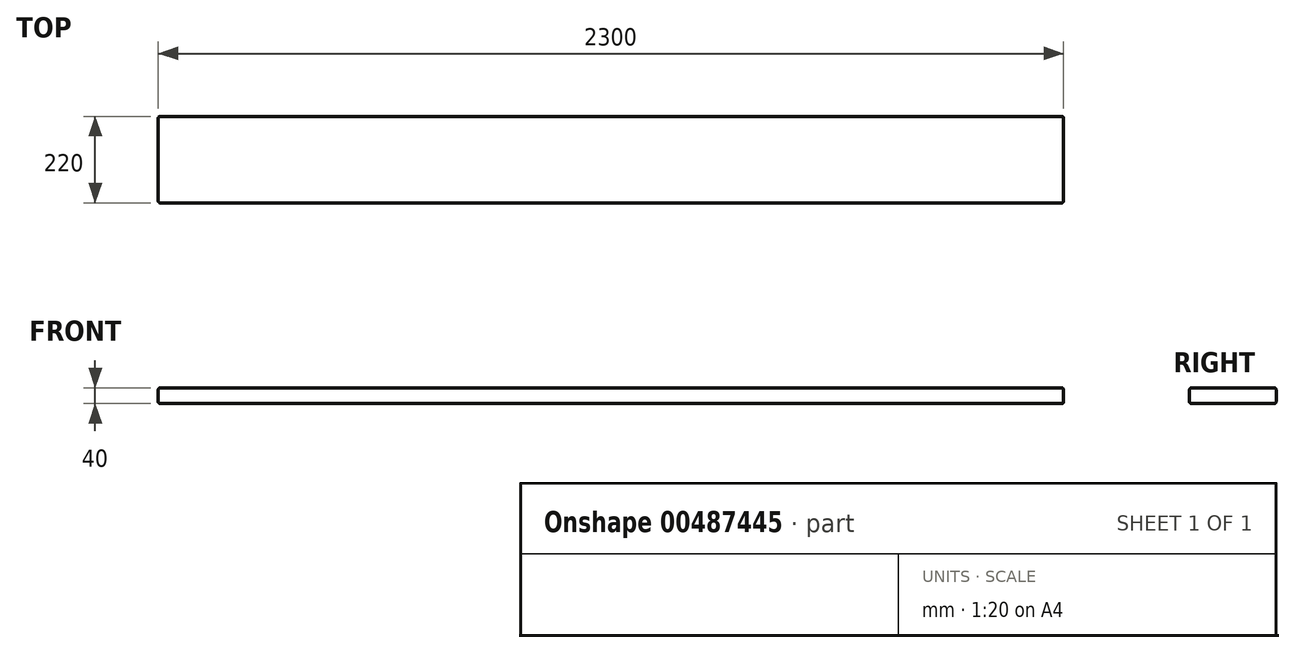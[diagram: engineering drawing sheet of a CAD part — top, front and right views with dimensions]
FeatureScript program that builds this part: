
annotation { "Feature Type Name" : "Feature", "Feature Type Description" : "" }
export const myFeature = defineFeature(function(context is Context, id is Id, definition is map)
    precondition{}
    {
        {
            var Q0;
            Q0=qCreatedBy(makeId("Right.planeOp"),FACE);
            var sketch = newSketch(context, id + "F0", { "sketchPlane" : qUnion([Q0])});
            skLineSegment(sketch, "E0.bottom", {"start": v(5, 0) * mm, "end": v(215, 0) * mm});
            skLineSegment(sketch, "E0.top", {"start": v(5, 40) * mm, "end": v(215, 40) * mm});
            skLineSegment(sketch, "E0.left", {"start": v(0, 5) * mm, "end": v(0, 35) * mm});
            skLineSegment(sketch, "E0.right", {"start": v(220, 5) * mm, "end": v(220, 35) * mm});
            skPoint(sketch, "E1.visualSharp", {"position": v(0, 40) * mm});
            skArc(sketch, "E1.filletArc", {"start": v(5, 40) * mm, "mid": v(1.46, 38.54) * mm, "end": v(0, 35) * mm});
            skPoint(sketch, "E2.visualSharp", {"position": v(0, 0) * mm});
            skArc(sketch, "E2.filletArc", {"start": v(0, 5) * mm, "mid": v(1.46, 1.46) * mm, "end": v(5, 0) * mm});
            skPoint(sketch, "E3.visualSharp", {"position": v(220, 0) * mm});
            skArc(sketch, "E3.filletArc", {"start": v(215, 0) * mm, "mid": v(218.54, 1.46) * mm, "end": v(220, 5) * mm});
            skPoint(sketch, "E4.visualSharp", {"position": v(220, 40) * mm});
            skArc(sketch, "E4.filletArc", {"start": v(220, 35) * mm, "mid": v(218.54, 38.54) * mm, "end": v(215, 40) * mm});
            skSolve(sketch);
        }
        {
            var Q0;
            Q0 = qSketchRegion(id + "F0", true);
            extrude(context, id + "F1", {"entities" : qUnion([Q0]), "oppositeDirection" : true, "depth" : 2300 * mm});
        }
        {
            var Q0;
            Q0=makeQuery(id+"F1.opExtrude","CAP_EDGE",EDGE,{"disambiguationData":[OSD([sQuery(id+"F0.wireOp",EDGE,"E0.top")])],"isStart":true});
            fillet(context, id + "F2", {"entities" : qUnion([Q0]), "radius" : 5 * mm, "tangentPropagation" : true, "allowEdgeOverflow" : false});
        }
        {
            var Q0;
            Q0=makeQuery(id+"F1.opExtrude","CAP_FACE",FACE,{"disambiguationData":[OSD([sQuery(id+"F0.wireOp",EDGE,"E0.bottom"),sQuery(id+"F0.wireOp",EDGE,"E0.top"),sQuery(id+"F0.wireOp",EDGE,"E0.left"),sQuery(id+"F0.wireOp",EDGE,"E0.right"),sQuery(id+"F0.wireOp",EDGE,"E1.filletArc"),sQuery(id+"F0.wireOp",EDGE,"E2.filletArc"),sQuery(id+"F0.wireOp",EDGE,"E3.filletArc"),sQuery(id+"F0.wireOp",EDGE,"E4.filletArc")])],"isStart":false});
            fillet(context, id + "F3", {"entities" : qUnion([Q0]), "radius" : 5 * mm, "tangentPropagation" : true, "allowEdgeOverflow" : false});
        }
    });
